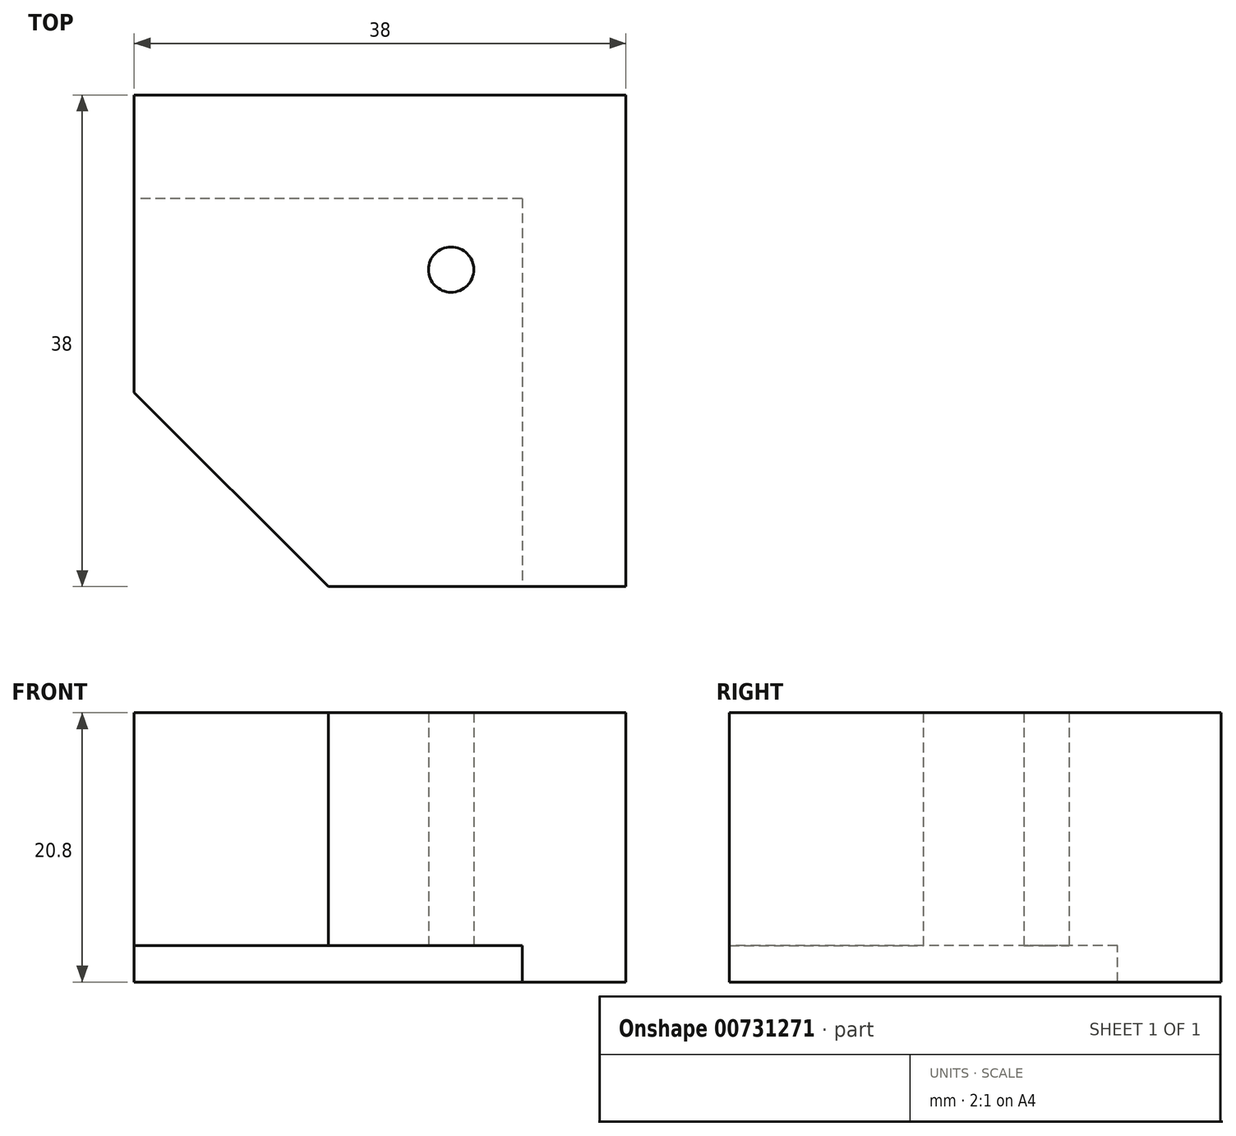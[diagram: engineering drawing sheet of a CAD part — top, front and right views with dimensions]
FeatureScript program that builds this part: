
annotation { "Feature Type Name" : "Feature", "Feature Type Description" : "" }
export const myFeature = defineFeature(function(context is Context, id is Id, definition is map)
    precondition{}
    {
        {
            var Q0;
            Q0=qCreatedBy(makeId("Top.planeOp"),FACE);
            var sketch = newSketch(context, id + "F0", { "sketchPlane" : qUnion([Q0])});
            skCircle(sketch, "E0", {"center": v(0, 0) * mm, "radius": 1.75 * mm});
            skCircle(sketch, "E1", {"center": v(0, 0) * mm, "radius": 5.5 * mm, "construction": true});
            skLineSegment(sketch, "E2", {"start": v(5.5, 0) * mm, "end": v(5.5, -24.5) * mm});
            skLineSegment(sketch, "E3", {"start": v(0, 5.5) * mm, "end": v(-24.5, 5.5) * mm});
            skLineSegment(sketch, "E4", {"start": v(-24.5, 5.5) * mm, "end": v(-24.5, -9.5) * mm});
            skLineSegment(sketch, "E5", {"start": v(5.5, -24.5) * mm, "end": v(-9.5, -24.5) * mm});
            skLineSegment(sketch, "E6", {"start": v(-9.5, -24.5) * mm, "end": v(-24.5, -9.5) * mm});
            skLineSegment(sketch, "E7", {"start": v(0, 5.5) * mm, "end": v(5.5, 5.5) * mm});
            skLineSegment(sketch, "E8", {"start": v(5.5, 5.5) * mm, "end": v(5.5, 0) * mm});
            skLineSegment(sketch, "E9.0", {"start": v(0, 13.5) * mm, "end": v(-24.5, 13.5) * mm});
            skLineSegment(sketch, "E9.1", {"start": v(0, 13.5) * mm, "end": v(13.5, 13.5) * mm});
            skLineSegment(sketch, "E9.2", {"start": v(13.5, 13.5) * mm, "end": v(13.5, 0) * mm});
            skLineSegment(sketch, "E9.3", {"start": v(13.5, 0) * mm, "end": v(13.5, -24.5) * mm});
            skLineSegment(sketch, "E10", {"start": v(-24.5, 13.5) * mm, "end": v(-24.5, 5.5) * mm});
            skLineSegment(sketch, "E11", {"start": v(5.5, -24.5) * mm, "end": v(13.5, -24.5) * mm});
            skSolve(sketch);
        }
        {
            var Q0;
            Q0=makeQuery(id+"F0.imprint","IMPRINT",FACE,{"disambiguationData":[TD([[makeQuery(id+"F0.imprint","IMPRINT",EDGE,{"derivedFrom":sQuery(id+"F0.wireOp",EDGE,"E0")}),-1.0]])]});
            var Q1;
            Q1=makeQuery(id+"F0.imprint","IMPRINT",FACE,{"disambiguationData":[TD([[makeQuery(id+"F0.imprint","IMPRINT",EDGE,{"derivedFrom":sQuery(id+"F0.wireOp",EDGE,"E2")}),1.0]])]});
            extrude(context, id + "F1", {"entities" : qUnion([Q0, Q1]), "depth" : 18 * mm, "offsetDistance" : 25 * mm});
        }
        {
            var Q0;
            Q0=makeQuery(id+"F0.imprint","IMPRINT",FACE,{"disambiguationData":[TD([[makeQuery(id+"F0.imprint","IMPRINT",EDGE,{"derivedFrom":sQuery(id+"F0.wireOp",EDGE,"E2")}),1.0]])]});
            extrude(context, id + "F2", {"entities" : qUnion([Q0]), "operationType" : NewBodyOperationType.ADD, "oppositeDirection" : true, "depth" : 2.8 * mm, "offsetDistance" : 25 * mm});
        }
        {
            var Q0;
            Q0=makeQuery(id+"F1.opExtrude","SWEPT_BODY",BODY,{"disambiguationData":[OSD([sQuery(id+"F0.wireOp",EDGE,"E0"),sQuery(id+"F0.wireOp",EDGE,"E4"),sQuery(id+"F0.wireOp",EDGE,"E5"),sQuery(id+"F0.wireOp",EDGE,"E6"),sQuery(id+"F0.wireOp",EDGE,"E9.0"),sQuery(id+"F0.wireOp",EDGE,"E9.1"),sQuery(id+"F0.wireOp",EDGE,"E9.2"),sQuery(id+"F0.wireOp",EDGE,"E9.3"),sQuery(id+"F0.wireOp",EDGE,"E10"),sQuery(id+"F0.wireOp",EDGE,"E11")])]});
            transform(context, id + "F3", {"entities" : qUnion([Q0]), "transformType" : TransformType.TRANSLATION_3D, "dx" : 0 * mm, "dy" : 0 * mm, "dz" : 0 * mm, "makeCopy" : true});
        }
    });
